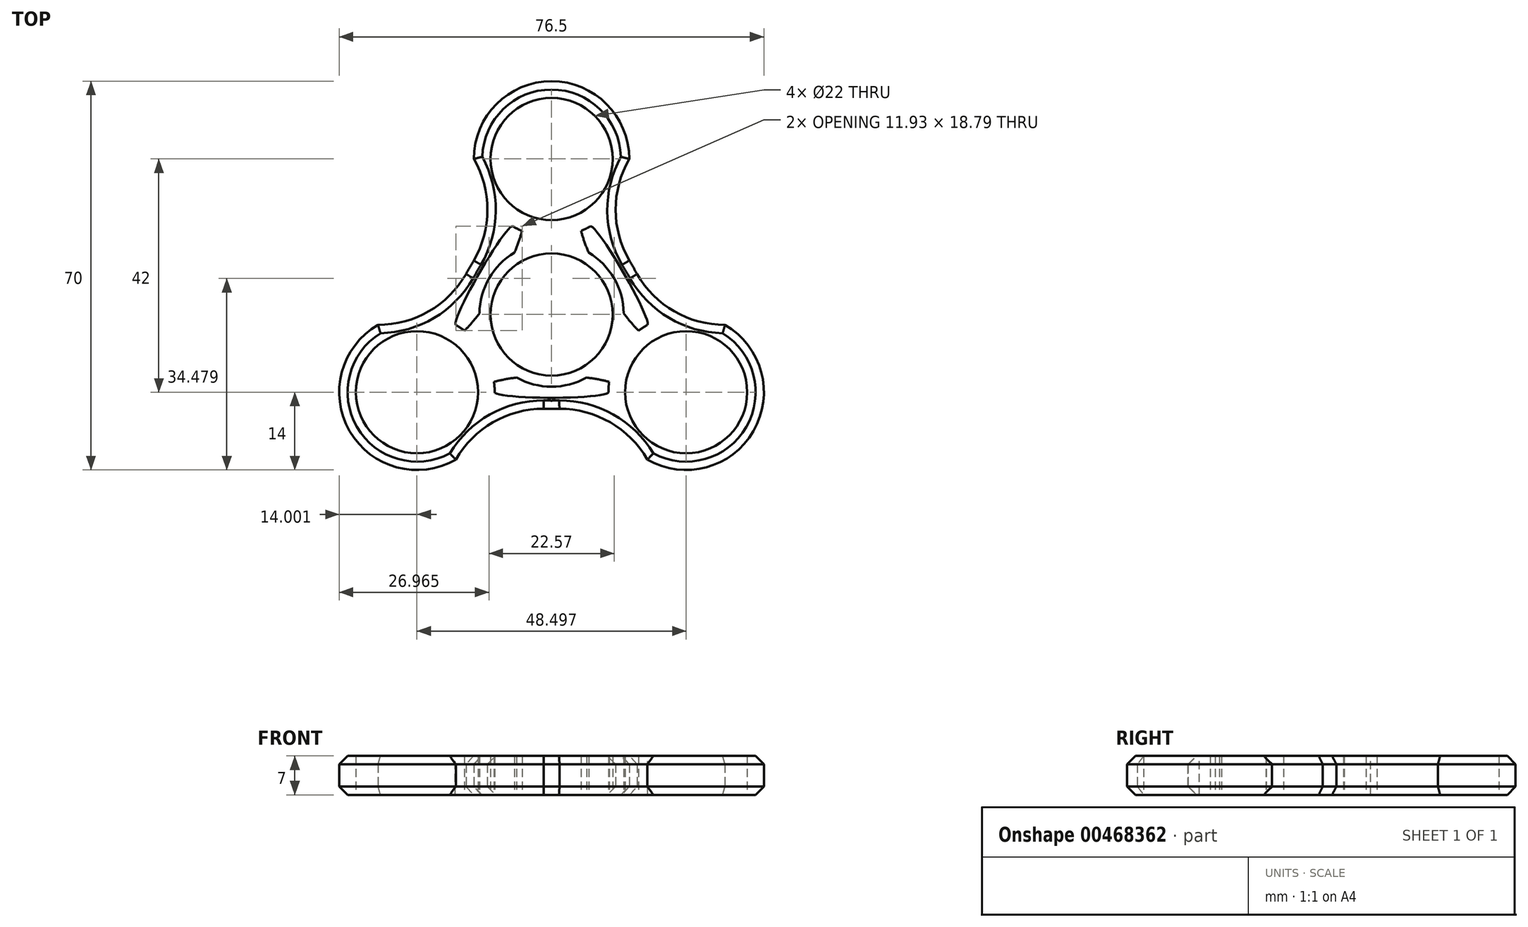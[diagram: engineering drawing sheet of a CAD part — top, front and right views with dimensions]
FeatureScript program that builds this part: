
annotation { "Feature Type Name" : "Feature", "Feature Type Description" : "" }
export const myFeature = defineFeature(function(context is Context, id is Id, definition is map)
    precondition{}
    {
        {
            var Q0;
            Q0=qCreatedBy(makeId("Top.planeOp"),FACE);
            var sketch = newSketch(context, id + "F0", { "sketchPlane" : qUnion([Q0])});
            skCircle(sketch, "E0", {"center": v(0, 0) * mm, "radius": 11 * mm});
            skCircle(sketch, "E1", {"center": v(0, 28) * mm, "radius": 11 * mm});
            skArc(sketch, "E2.0", {"start": v(14, 28) * mm, "mid": v(0, 42) * mm, "end": v(-14, 28) * mm});
            skArc(sketch, "E3.0", {"start": v(6.68, 11.15) * mm, "mid": v(-11.26, -6.5) * mm, "end": v(13, 0.21) * mm});
            skArc(sketch, "E4.1.0", {"start": v(-31.25, -1.88) * mm, "mid": v(-36.37, -21) * mm, "end": v(-17.25, -26.12) * mm});
            skCircle(sketch, "E4.1.1", {"center": v(-24.25, -14) * mm, "radius": 11 * mm});
            skArc(sketch, "E4.2.0", {"start": v(23.24, -0.04) * mm, "mid": v(12.12, -7) * mm, "end": v(11.65, -20.1) * mm});
            skCircle(sketch, "E4.2.1", {"center": v(24.25, -14) * mm, "radius": 11 * mm});
            skPoint(sketch, "E5", {"position": v(12.12, 7) * mm});
            skPoint(sketch, "E6", {"position": v(5.5, 18.47) * mm});
            skPoint(sketch, "E7", {"position": v(7, 15.88) * mm});
            skPoint(sketch, "E8", {"position": v(9.53, 5.5) * mm});
            skPoint(sketch, "E9", {"position": v(11.26, 6.5) * mm});
            skEllipse(sketch, "E10", {"center": v(12.12, 7) * mm, "majorRadius": 1 * mm, "minorRadius": 10.25 * mm, "majorAxis": v(-0.87, -0.5)});
            skEllipticalArc(sketch, "E11", {});
            skEllipticalArc(sketch, "E12.1.0", {});
            skEllipse(sketch, "E12.1.1", {"center": v(-12.12, 7) * mm, "majorRadius": 1 * mm, "minorRadius": 10.25 * mm, "majorAxis": v(0.87, -0.5)});
            skEllipticalArc(sketch, "E12.2.0", {});
            skEllipse(sketch, "E12.2.1", {"center": v(0, -14) * mm, "majorRadius": 1 * mm, "minorRadius": 10.25 * mm, "majorAxis": v(0, 1)});
            skEllipticalArc(sketch, "E13.trimOffspring", {});
            skEllipticalArc(sketch, "E14.trimOffspring", {});
            skEllipticalArc(sketch, "E15.trimOffspring", {});
            skEllipticalArc(sketch, "E16.trimOffspring", {});
            skEllipticalArc(sketch, "E17.trimOffspring", {});
            skEllipticalArc(sketch, "E18.trimOffspring", {});
            skLineSegment(sketch, "E19", {"start": v(0, 28) * mm, "end": v(14, 28) * mm});
            skArc(sketch, "E20", {"start": v(14, 28) * mm, "mid": v(11.54, 18.86) * mm, "end": v(14, 9.72) * mm});
            skArc(sketch, "E21.MirrorCS", {"start": v(31.25, -1.88) * mm, "mid": v(22.1, 0.57) * mm, "end": v(15.42, 7.27) * mm});
            skArc(sketch, "E22.1.0", {"start": v(-31.25, -1.88) * mm, "mid": v(-22.1, 0.57) * mm, "end": v(-15.42, 7.27) * mm});
            skArc(sketch, "E22.1.1", {"start": v(-14, 28) * mm, "mid": v(-11.54, 18.86) * mm, "end": v(-14, 9.72) * mm});
            skArc(sketch, "E22.2.0", {"start": v(17.25, -26.12) * mm, "mid": v(10.56, -19.43) * mm, "end": v(1.42, -16.98) * mm});
            skArc(sketch, "E22.2.1", {"start": v(-17.25, -26.12) * mm, "mid": v(-10.56, -19.43) * mm, "end": v(-1.42, -16.98) * mm});
            skArc(sketch, "E23.trimOffspring", {"start": v(-11.59, 20.14) * mm, "mid": v(0, 14) * mm, "end": v(11.59, 20.14) * mm});
            skArc(sketch, "E24.trimOffspring", {"start": v(-11.65, -20.1) * mm, "mid": v(-12.12, -7) * mm, "end": v(-23.24, -0.04) * mm});
            skArc(sketch, "E25.trimOffspring", {"start": v(17.25, -26.12) * mm, "mid": v(36.37, -21) * mm, "end": v(31.25, -1.88) * mm});
            skArc(sketch, "E26", {"start": v(6.68, 11.15) * mm, "mid": v(11.26, 6.5) * mm, "end": v(13, 0.21) * mm});
            const initialGuessF0  = {"E11": [0.012124355652982135, 0.007, -0.8660254037844389, -0.5, 0.003, 0.013248711305964282, 5.383723669402354, 5.78629307168484], "E12.1.0": [-0.01212435565298213, 0.007, 0.8660254037844383, -0.5, 0.003, 0.013248711305964282, 0.4968922354947489, 0.8994616377772289], "E12.2.0": [0, -0.014, 0, 1, 0.003, 0.013248711305964282, 5.383723669402354, 5.78629307168483], "E13.trimOffspring": [0.012124355652982135, 0.007, -0.8660254037844389, -0.5, 0.003, 0.013248711305964282, 2.2421310158125616, 4.0410542913670255], "E14.trimOffspring": [0.012124355652982135, 0.007, -0.8660254037844389, -0.5, 0.003, 0.013248711305964282, 0.4968922354947516, 0.8994616377772324], "E15.trimOffspring": [0, -0.014, 0, 1, 0.003, 0.013248711305964282, 0.4968922354947498, 0.8994616377772324], "E16.trimOffspring": [0, -0.014, 0, 1, 0.003, 0.013248711305964282, 2.2421310158125616, 4.041054291367027], "E17.trimOffspring": [-0.01212435565298213, 0.007, 0.8660254037844383, -0.5, 0.003, 0.013248711305964282, 2.2421310158125642, 4.0410542913670255], "E18.trimOffspring": [-0.01212435565298213, 0.007, 0.8660254037844383, -0.5, 0.003, 0.013248711305964282, 5.383723669402354, 5.786293071684838]};
            skSetInitialGuess(sketch, initialGuessF0);
            skSolve(sketch);
        }
        {
            var Q0;
            Q0=makeQuery(id+"F0.imprint","IMPRINT",FACE,{"disambiguationData":[TD([[makeQuery(id+"F0.imprint","IMPRINT",EDGE,{"derivedFrom":sQuery(id+"F0.wireOp",EDGE,"E1")}),-1.0]])]});
            var Q1;
            {var subQ0=sQuery(id+"F0.wireOp",EDGE,"E23.trimOffspring");var subQ1=sQuery(id+"F0.wireOp",EDGE,"E17.trimOffspring");var subQ2=makeQuery(id+"F0.imprint","INTERSECT",VERTEX,{"derivedFrom":[subQ1,subQ0]});Q1=makeQuery(id+"F0.imprint","IMPRINT",FACE,{"disambiguationData":[TD([[makeQuery(id+"F0.imprint","IMPRINT",EDGE,{"disambiguationData":[TD([[subQ2,-1.0]])],"derivedFrom":subQ1}),-1.0]])]});}
            var Q2;
            {var subQ0=sQuery(id+"F0.wireOp",EDGE,"E24.trimOffspring");var subQ7=sQuery(id+"F0.wireOp",EDGE,"E12.1.1");var subQ8=makeQuery(id+"F0.imprint","INTERSECT",VERTEX,{"derivedFrom":[subQ7,subQ0]});Q2=makeQuery(id+"F0.imprint","IMPRINT",FACE,{"disambiguationData":[TD([[makeQuery(id+"F0.imprint","IMPRINT",EDGE,{"disambiguationData":[TD([[subQ8,1.0]])],"derivedFrom":subQ7}),-1.0]])]});}
            var Q3;
            {var subQ0=sQuery(id+"F0.wireOp",EDGE,"E24.trimOffspring");var subQ1=sQuery(id+"F0.wireOp",EDGE,"E17.trimOffspring");var subQ2=makeQuery(id+"F0.imprint","INTERSECT",VERTEX,{"derivedFrom":[subQ1,subQ0]});Q3=makeQuery(id+"F0.imprint","IMPRINT",FACE,{"disambiguationData":[TD([[makeQuery(id+"F0.imprint","IMPRINT",EDGE,{"disambiguationData":[TD([[subQ2,1.0]])],"derivedFrom":subQ1}),-1.0]])]});}
            var Q4;
            {var subQ10=sQuery(id+"F0.wireOp",EDGE,"E4.1.0");Q4=makeQuery(id+"F0.imprint","IMPRINT",FACE,{"disambiguationData":[TD([[makeQuery(id+"F0.imprint","IMPRINT",EDGE,{"derivedFrom":subQ10}),1.0]])]});}
            var Q5;
            {var subQ0=sQuery(id+"F0.wireOp",EDGE,"E24.trimOffspring");var subQ1=sQuery(id+"F0.wireOp",EDGE,"E16.trimOffspring");var subQ2=makeQuery(id+"F0.imprint","INTERSECT",VERTEX,{"derivedFrom":[subQ1,subQ0]});Q5=makeQuery(id+"F0.imprint","IMPRINT",FACE,{"disambiguationData":[TD([[makeQuery(id+"F0.imprint","IMPRINT",EDGE,{"disambiguationData":[TD([[subQ2,-1.0]])],"derivedFrom":subQ1}),-1.0]])]});}
            var Q6;
            {var subQ0=sQuery(id+"F0.wireOp",EDGE,"E16.trimOffspring");var subQ4=sQuery(id+"F0.wireOp",EDGE,"E4.2.0");var subQ9=makeQuery(id+"F0.imprint","INTERSECT",VERTEX,{"derivedFrom":[subQ4,subQ0]});Q6=makeQuery(id+"F0.imprint","IMPRINT",FACE,{"disambiguationData":[TD([[makeQuery(id+"F0.imprint","IMPRINT",EDGE,{"disambiguationData":[TD([[subQ9,1.0]])],"derivedFrom":subQ4}),-1.0]])]});}
            var Q7;
            {var subQ0=sQuery(id+"F0.wireOp",EDGE,"E22.2.0");var subQ1=sQuery(id+"F0.wireOp",EDGE,"E4.2.0");var subQ2=makeQuery(id+"F0.imprint","INTERSECT",VERTEX,{"derivedFrom":[subQ1,subQ0]});Q7=makeQuery(id+"F0.imprint","IMPRINT",FACE,{"disambiguationData":[TD([[makeQuery(id+"F0.imprint","IMPRINT",EDGE,{"disambiguationData":[TD([[subQ2,1.0]])],"derivedFrom":subQ1}),-1.0]])]});}
            var Q8;
            Q8=makeQuery(id+"F0.imprint","IMPRINT",FACE,{"disambiguationData":[TD([[makeQuery(id+"F0.imprint","IMPRINT",EDGE,{"derivedFrom":sQuery(id+"F0.wireOp",EDGE,"E4.2.1")}),-1.0]])]});
            var Q9;
            {var subQ0=sQuery(id+"F0.wireOp",EDGE,"E21.MirrorCS");var subQ1=sQuery(id+"F0.wireOp",EDGE,"E4.2.0");var subQ2=makeQuery(id+"F0.imprint","INTERSECT",VERTEX,{"derivedFrom":[subQ1,subQ0]});Q9=makeQuery(id+"F0.imprint","IMPRINT",FACE,{"disambiguationData":[TD([[makeQuery(id+"F0.imprint","IMPRINT",EDGE,{"disambiguationData":[TD([[subQ2,-1.0]])],"derivedFrom":subQ1}),-1.0]])]});}
            var Q10;
            {var subQ0=sQuery(id+"F0.wireOp",EDGE,"E23.trimOffspring");var subQ1=sQuery(id+"F0.wireOp",EDGE,"E13.trimOffspring");var subQ2=makeQuery(id+"F0.imprint","INTERSECT",VERTEX,{"derivedFrom":[subQ1,subQ0]});Q10=makeQuery(id+"F0.imprint","IMPRINT",FACE,{"disambiguationData":[TD([[makeQuery(id+"F0.imprint","IMPRINT",EDGE,{"disambiguationData":[TD([[subQ2,1.0]])],"derivedFrom":subQ1}),-1.0]])]});}
            var Q11;
            {var subQ0=sQuery(id+"F0.wireOp",EDGE,"E13.trimOffspring");var subQ1=sQuery(id+"F0.wireOp",EDGE,"E4.2.0");var subQ2=makeQuery(id+"F0.imprint","INTERSECT",VERTEX,{"derivedFrom":[subQ1,subQ0]});Q11=makeQuery(id+"F0.imprint","IMPRINT",FACE,{"disambiguationData":[TD([[makeQuery(id+"F0.imprint","IMPRINT",EDGE,{"disambiguationData":[TD([[subQ2,-1.0]])],"derivedFrom":subQ1}),-1.0]])]});}
            var Q12;
            {var subQ0=sQuery(id+"F0.wireOp",EDGE,"E11");Q12=makeQuery(id+"F0.imprint","IMPRINT",FACE,{"disambiguationData":[TD([[makeQuery(id+"F0.imprint","IMPRINT",EDGE,{"derivedFrom":subQ0}),-1.0]])]});}
            var Q13;
            Q13=makeQuery(id+"F0.imprint","IMPRINT",FACE,{"disambiguationData":[TD([[makeQuery(id+"F0.imprint","IMPRINT",EDGE,{"derivedFrom":sQuery(id+"F0.wireOp",EDGE,"E0")}),-1.0]])]});
            var Q14;
            {var subQ2=sQuery(id+"F0.wireOp",EDGE,"E12.2.0");Q14=makeQuery(id+"F0.imprint","IMPRINT",FACE,{"disambiguationData":[TD([[makeQuery(id+"F0.imprint","IMPRINT",EDGE,{"derivedFrom":subQ2}),-1.0]])]});}
            var Q15;
            {var subQ0=sQuery(id+"F0.wireOp",EDGE,"E15.trimOffspring");Q15=makeQuery(id+"F0.imprint","IMPRINT",FACE,{"disambiguationData":[TD([[makeQuery(id+"F0.imprint","IMPRINT",EDGE,{"derivedFrom":subQ0}),-1.0]])]});}
            extrude(context, id + "F1", {"entities" : qUnion([Q0, Q1, Q2, Q3, Q4, Q5, Q6, Q7, Q8, Q9, Q10, Q11, Q12, Q13, Q14, Q15]), "endBound" : BoundingType.SYMMETRIC, "depth" : 7 * mm});
        }
        {
            var Q0;
            Q0=makeQuery(id+"F1.opExtrude","CAP_EDGE",EDGE,{"disambiguationData":[OSD([sQuery(id+"F0.wireOp",EDGE,"E2.0")])],"isStart":false});
            var Q1;
            Q1=makeQuery(id+"F1.opExtrude","CAP_EDGE",EDGE,{"disambiguationData":[OSD([sQuery(id+"F0.wireOp",EDGE,"E22.1.1")])],"isStart":false});
            var Q2;
            Q2=makeQuery(id+"F1.opExtrude","CAP_EDGE",EDGE,{"disambiguationData":[OSD([sQuery(id+"F0.wireOp",EDGE,"E17.trimOffspring")])],"isStart":false});
            var Q3;
            Q3=makeQuery(id+"F1.opExtrude","CAP_EDGE",EDGE,{"disambiguationData":[OSD([sQuery(id+"F0.wireOp",EDGE,"E22.1.0")])],"isStart":false});
            var Q4;
            Q4=makeQuery(id+"F1.opExtrude","CAP_EDGE",EDGE,{"disambiguationData":[OSD([sQuery(id+"F0.wireOp",EDGE,"E4.1.0")])],"isStart":false});
            var Q5;
            Q5=makeQuery(id+"F1.opExtrude","CAP_EDGE",EDGE,{"disambiguationData":[OSD([sQuery(id+"F0.wireOp",EDGE,"E22.2.1")])],"isStart":false});
            var Q6;
            Q6=makeQuery(id+"F1.opExtrude","CAP_EDGE",EDGE,{"disambiguationData":[OSD([sQuery(id+"F0.wireOp",EDGE,"E16.trimOffspring")])],"isStart":false});
            var Q7;
            Q7=makeQuery(id+"F1.opExtrude","CAP_EDGE",EDGE,{"disambiguationData":[OSD([sQuery(id+"F0.wireOp",EDGE,"E22.2.0")])],"isStart":false});
            var Q8;
            Q8=makeQuery(id+"F1.opExtrude","CAP_EDGE",EDGE,{"disambiguationData":[OSD([sQuery(id+"F0.wireOp",EDGE,"E25.trimOffspring")])],"isStart":false});
            var Q9;
            Q9=makeQuery(id+"F1.opExtrude","CAP_EDGE",EDGE,{"disambiguationData":[OSD([sQuery(id+"F0.wireOp",EDGE,"E21.MirrorCS")])],"isStart":false});
            var Q10;
            Q10=makeQuery(id+"F1.opExtrude","CAP_EDGE",EDGE,{"disambiguationData":[OSD([sQuery(id+"F0.wireOp",EDGE,"E13.trimOffspring")])],"isStart":false});
            var Q11;
            Q11=makeQuery(id+"F1.opExtrude","CAP_EDGE",EDGE,{"disambiguationData":[OSD([sQuery(id+"F0.wireOp",EDGE,"E20")])],"isStart":false});
            var Q12;
            Q12=makeQuery(id+"F1.opExtrude","CAP_EDGE",EDGE,{"disambiguationData":[OSD([sQuery(id+"F0.wireOp",EDGE,"E4.1.0")])],"isStart":true});
            var Q13;
            Q13=makeQuery(id+"F1.opExtrude","CAP_EDGE",EDGE,{"disambiguationData":[OSD([sQuery(id+"F0.wireOp",EDGE,"E22.2.1")])],"isStart":true});
            var Q14;
            Q14=makeQuery(id+"F1.opExtrude","CAP_EDGE",EDGE,{"disambiguationData":[OSD([sQuery(id+"F0.wireOp",EDGE,"E16.trimOffspring")])],"isStart":true});
            var Q15;
            Q15=makeQuery(id+"F1.opExtrude","CAP_EDGE",EDGE,{"disambiguationData":[OSD([sQuery(id+"F0.wireOp",EDGE,"E22.2.0")])],"isStart":true});
            var Q16;
            Q16=makeQuery(id+"F1.opExtrude","CAP_EDGE",EDGE,{"disambiguationData":[OSD([sQuery(id+"F0.wireOp",EDGE,"E25.trimOffspring")])],"isStart":true});
            var Q17;
            Q17=makeQuery(id+"F1.opExtrude","CAP_EDGE",EDGE,{"disambiguationData":[OSD([sQuery(id+"F0.wireOp",EDGE,"E21.MirrorCS")])],"isStart":true});
            var Q18;
            Q18=makeQuery(id+"F1.opExtrude","CAP_EDGE",EDGE,{"disambiguationData":[OSD([sQuery(id+"F0.wireOp",EDGE,"E13.trimOffspring")])],"isStart":true});
            var Q19;
            Q19=makeQuery(id+"F1.opExtrude","CAP_EDGE",EDGE,{"disambiguationData":[OSD([sQuery(id+"F0.wireOp",EDGE,"E20")])],"isStart":true});
            var Q20;
            Q20=makeQuery(id+"F1.opExtrude","CAP_EDGE",EDGE,{"disambiguationData":[OSD([sQuery(id+"F0.wireOp",EDGE,"E2.0")])],"isStart":true});
            var Q21;
            Q21=makeQuery(id+"F1.opExtrude","CAP_EDGE",EDGE,{"disambiguationData":[OSD([sQuery(id+"F0.wireOp",EDGE,"E22.1.1")])],"isStart":true});
            var Q22;
            Q22=makeQuery(id+"F1.opExtrude","CAP_EDGE",EDGE,{"disambiguationData":[OSD([sQuery(id+"F0.wireOp",EDGE,"E17.trimOffspring")])],"isStart":true});
            var Q23;
            Q23=makeQuery(id+"F1.opExtrude","CAP_EDGE",EDGE,{"disambiguationData":[OSD([sQuery(id+"F0.wireOp",EDGE,"E22.1.0")])],"isStart":true});
            chamfer(context, id + "F2", {"entities" : qUnion([Q0, Q1, Q2, Q3, Q4, Q5, Q6, Q7, Q8, Q9, Q10, Q11, Q12, Q13, Q14, Q15, Q16, Q17, Q18, Q19, Q20, Q21, Q22, Q23]), "width" : 1.5 * mm, "tangentPropagation" : true});
        }
    });
